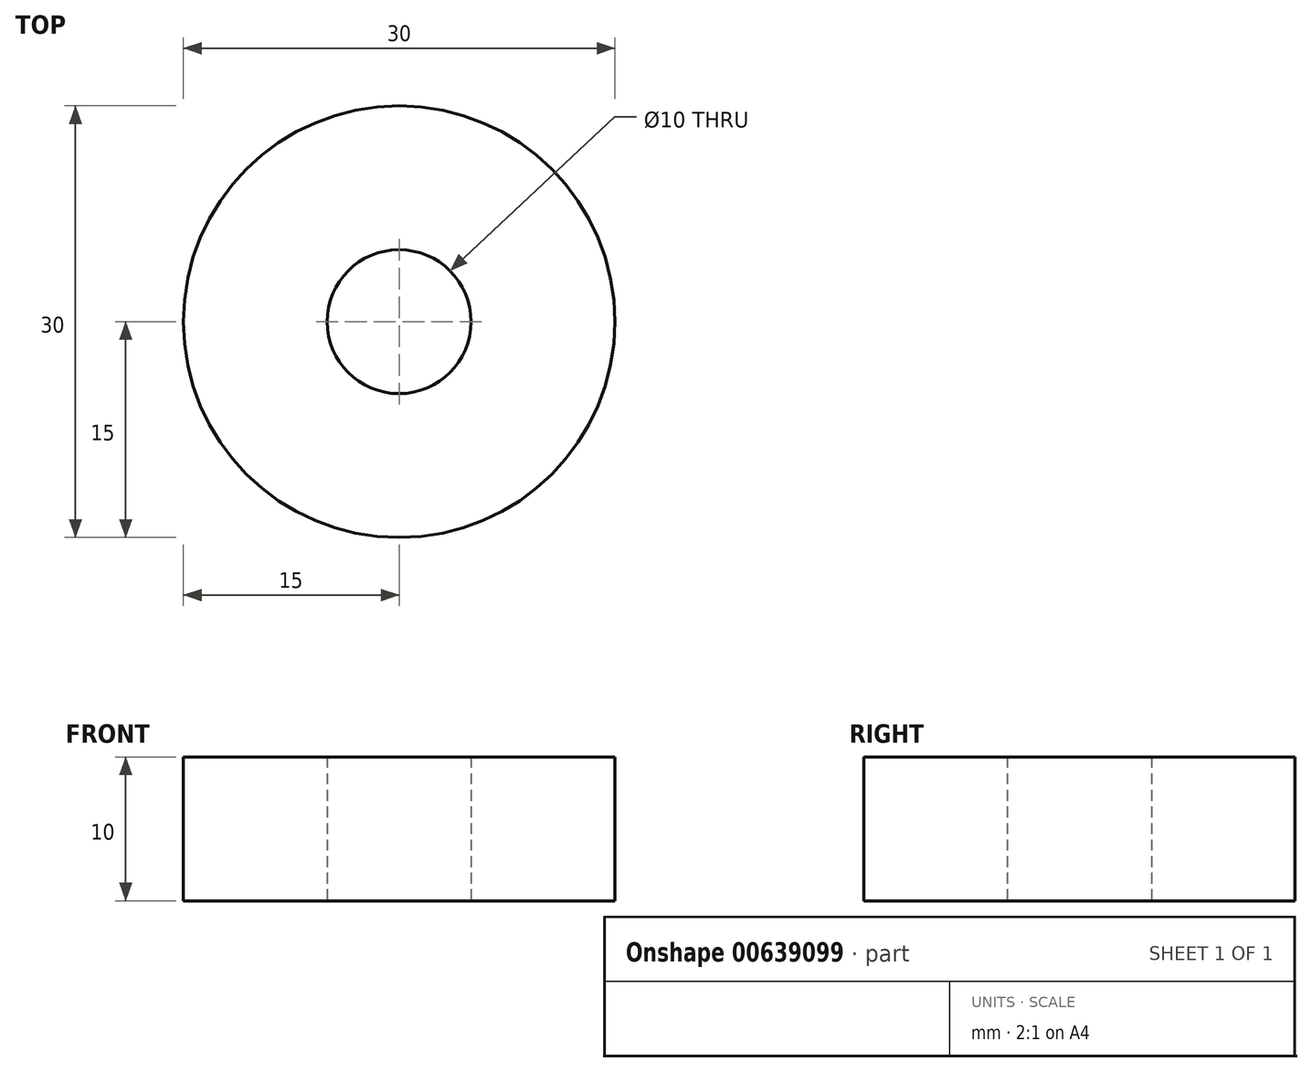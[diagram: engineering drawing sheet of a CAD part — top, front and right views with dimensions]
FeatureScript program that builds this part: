
annotation { "Feature Type Name" : "Feature", "Feature Type Description" : "" }
export const myFeature = defineFeature(function(context is Context, id is Id, definition is map)
    precondition{}
    {
        {
            var Q0;
            Q0=qCreatedBy(makeId("Top.planeOp"),FACE);
            var sketch = newSketch(context, id + "F0", { "sketchPlane" : qUnion([Q0])});
            skCircle(sketch, "E0", {"center": v(0, 0) * mm, "radius": 5 * mm});
            skCircle(sketch, "E1", {"center": v(0, 0) * mm, "radius": 15 * mm});
            skSolve(sketch);
        }
        {
            var Q0;
            Q0=makeQuery(id+"F0.imprint","IMPRINT",FACE,{"disambiguationData":[TD([[makeQuery(id+"F0.imprint","IMPRINT",EDGE,{"derivedFrom":sQuery(id+"F0.wireOp",EDGE,"E0")}),-1.0]])]});
            extrude(context, id + "F1", {"entities" : qUnion([Q0]), "depth" : 10 * mm, "offsetDistance" : 25 * mm});
        }
    });
